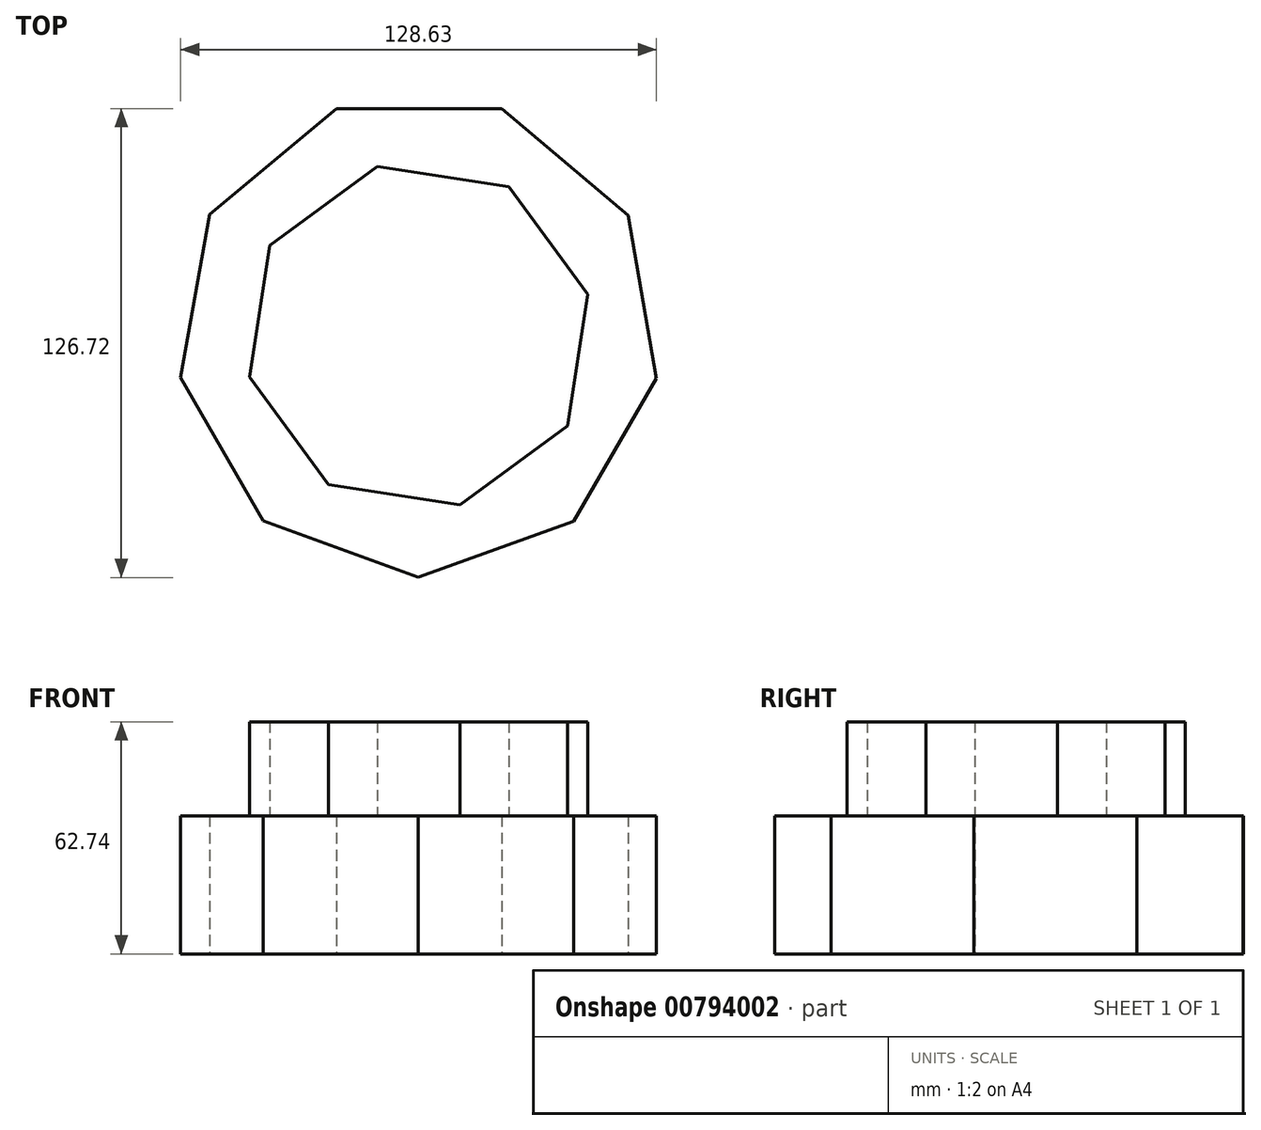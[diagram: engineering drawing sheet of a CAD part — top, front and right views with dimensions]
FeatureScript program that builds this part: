
annotation { "Feature Type Name" : "Feature", "Feature Type Description" : "" }
export const myFeature = defineFeature(function(context is Context, id is Id, definition is map)
    precondition{}
    {
        {
            var Q0;
            Q0=qCreatedBy(makeId("Top.planeOp"),FACE);
            var sketch = newSketch(context, id + "F0", { "sketchPlane" : qUnion([Q0])});
            skCircle(sketch, "E0.cCircle", {"center": v(0, 0) * mm, "radius": 61.37 * mm, "construction": true});
            skLineSegment(sketch, "E0.0", {"start": v(64.3, -11.46) * mm, "end": v(41.88, -50.1) * mm});
            skLineSegment(sketch, "E0.1", {"start": v(41.88, -50.1) * mm, "end": v(-0.12, -65.3) * mm});
            skLineSegment(sketch, "E0.2", {"start": v(-0.12, -65.3) * mm, "end": v(-42.07, -49.95) * mm});
            skLineSegment(sketch, "E0.3", {"start": v(-42.07, -49.95) * mm, "end": v(-64.34, -11.22) * mm});
            skLineSegment(sketch, "E0.4", {"start": v(-64.34, -11.22) * mm, "end": v(-56.5, 32.76) * mm});
            skLineSegment(sketch, "E0.5", {"start": v(-56.5, 32.76) * mm, "end": v(-22.22, 61.41) * mm});
            skLineSegment(sketch, "E0.6", {"start": v(-22.22, 61.41) * mm, "end": v(22.45, 61.33) * mm});
            skLineSegment(sketch, "E0.7", {"start": v(22.45, 61.33) * mm, "end": v(56.62, 32.55) * mm});
            skLineSegment(sketch, "E0.8", {"start": v(56.62, 32.55) * mm, "end": v(64.3, -11.46) * mm});
            skPoint(sketch, "E0.0.midPoint", {"position": v(53.09, -30.79) * mm});
            skSolve(sketch);
        }
        {
            var Q0;
            Q0 = qSketchRegion(id + "F0", true);
            extrude(context, id + "F1", {"entities" : qUnion([Q0]), "depth" : 37.34 * mm, "offsetDistance" : 25.4 * mm});
        }
        {
            var Q0;
            Q0=makeQuery(id+"F1.opExtrude","CAP_FACE",FACE,{"disambiguationData":[OSD([sQuery(id+"F0.wireOp",EDGE,"E0.0"),sQuery(id+"F0.wireOp",EDGE,"E0.1"),sQuery(id+"F0.wireOp",EDGE,"E0.2"),sQuery(id+"F0.wireOp",EDGE,"E0.3"),sQuery(id+"F0.wireOp",EDGE,"E0.4"),sQuery(id+"F0.wireOp",EDGE,"E0.5"),sQuery(id+"F0.wireOp",EDGE,"E0.6"),sQuery(id+"F0.wireOp",EDGE,"E0.7"),sQuery(id+"F0.wireOp",EDGE,"E0.8")])],"isStart":false});
            var sketch = newSketch(context, id + "F2", { "sketchPlane" : qUnion([Q0])});
            skCircle(sketch, "E1.cCircle", {"center": v(0, 0) * mm, "radius": 43.47 * mm, "construction": true});
            skLineSegment(sketch, "E1.0", {"start": v(-40.23, 24.39) * mm, "end": v(-11.2, 45.7) * mm});
            skLineSegment(sketch, "E1.1", {"start": v(-11.2, 45.7) * mm, "end": v(24.39, 40.23) * mm});
            skLineSegment(sketch, "E1.2", {"start": v(24.39, 40.23) * mm, "end": v(45.7, 11.2) * mm});
            skLineSegment(sketch, "E1.3", {"start": v(45.7, 11.2) * mm, "end": v(40.23, -24.39) * mm});
            skLineSegment(sketch, "E1.4", {"start": v(40.23, -24.39) * mm, "end": v(11.2, -45.7) * mm});
            skLineSegment(sketch, "E1.5", {"start": v(11.2, -45.7) * mm, "end": v(-24.39, -40.23) * mm});
            skLineSegment(sketch, "E1.6", {"start": v(-24.39, -40.23) * mm, "end": v(-45.7, -11.2) * mm});
            skLineSegment(sketch, "E1.7", {"start": v(-45.7, -11.2) * mm, "end": v(-40.23, 24.39) * mm});
            skPoint(sketch, "E1.0.midPoint", {"position": v(-25.72, 35.04) * mm});
            skSolve(sketch);
        }
        {
            var Q0;
            Q0 = qSketchRegion(id + "F2", true);
            extrude(context, id + "F3", {"entities" : qUnion([Q0]), "operationType" : NewBodyOperationType.ADD, "depth" : 25.4 * mm, "offsetDistance" : 25.4 * mm});
        }
    });
